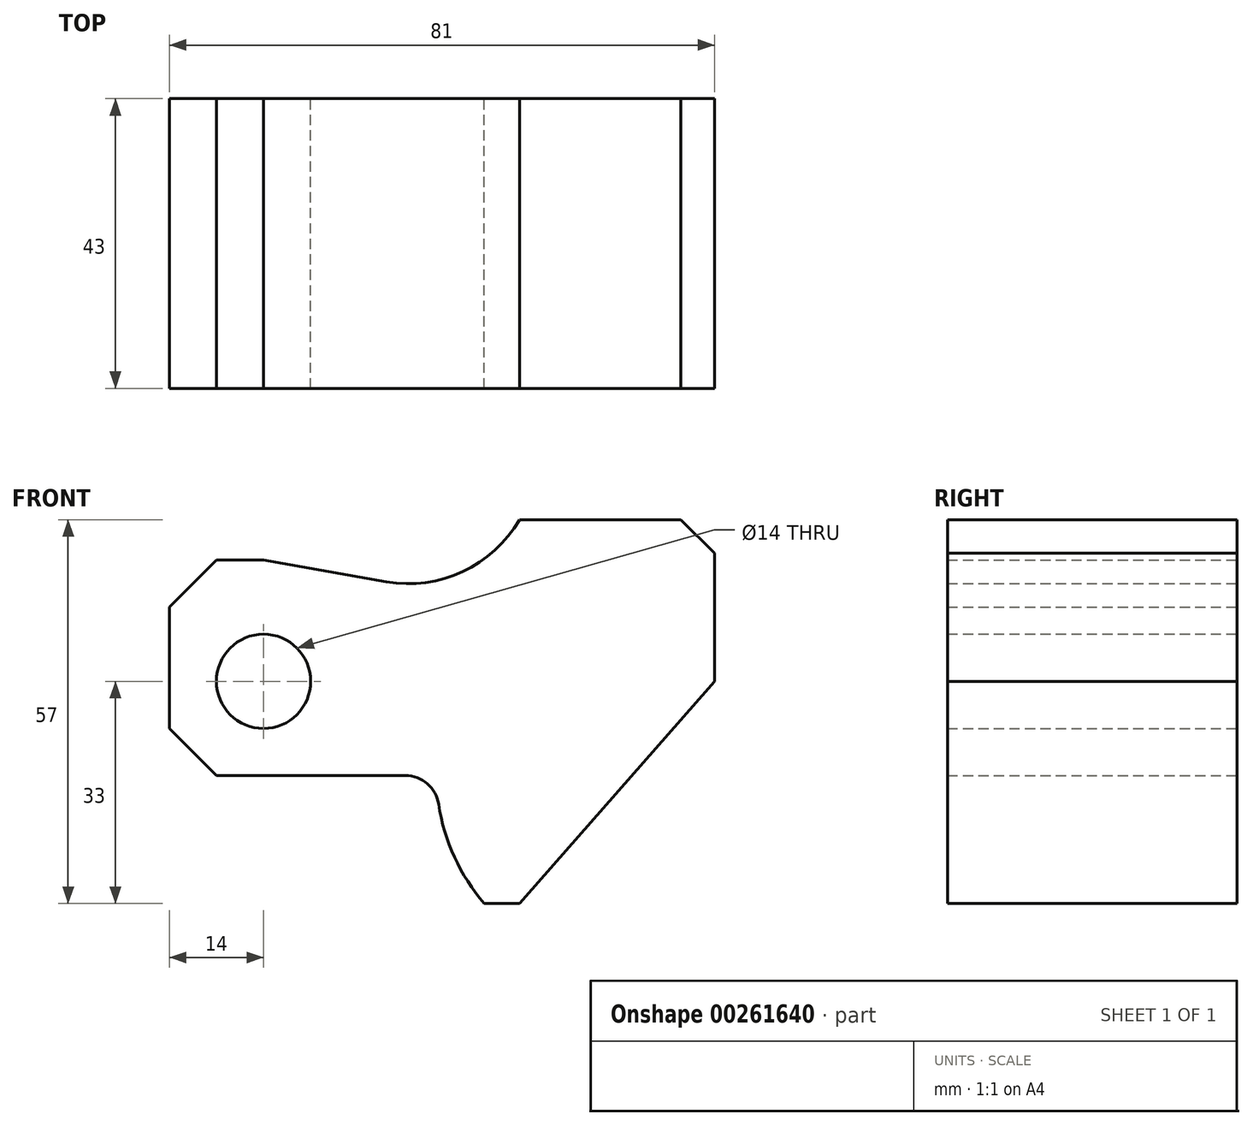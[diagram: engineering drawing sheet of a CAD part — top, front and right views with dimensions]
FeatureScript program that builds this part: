
annotation { "Feature Type Name" : "Feature", "Feature Type Description" : "" }
export const myFeature = defineFeature(function(context is Context, id is Id, definition is map)
    precondition{}
    {
        {
            var Q0;
            Q0=qCreatedBy(makeId("Front.planeOp"),FACE);
            var sketch = newSketch(context, id + "F0", { "sketchPlane" : qUnion([Q0])});
            skLineSegment(sketch, "E0", {"start": v(0, -18.6) * mm, "end": v(0, 28.52) * mm, "construction": true});
            skLineSegment(sketch, "E1", {"start": v(-26.7, 0) * mm, "end": v(26.52, 0) * mm, "construction": true});
            skCircle(sketch, "E2", {"center": v(0, 0) * mm, "radius": 7 * mm});
            skLineSegment(sketch, "E3", {"start": v(-14, 11) * mm, "end": v(-14, -7) * mm});
            skLineSegment(sketch, "E4", {"start": v(-14, -7) * mm, "end": v(-7, -14) * mm});
            skLineSegment(sketch, "E5", {"start": v(-7, -14) * mm, "end": v(21.07, -14) * mm});
            skLineSegment(sketch, "E6", {"start": v(-7, 18) * mm, "end": v(-14, 11) * mm});
            skLineSegment(sketch, "E7", {"start": v(-7, 18) * mm, "end": v(0, 18) * mm});
            skLineSegment(sketch, "E8", {"start": v(0, 18) * mm, "end": v(18.24, 14.78) * mm});
            skLineSegment(sketch, "E9", {"start": v(32.79, -33) * mm, "end": v(38, -33) * mm});
            skLineSegment(sketch, "E10", {"start": v(67, 0) * mm, "end": v(67, 19) * mm});
            skLineSegment(sketch, "E11", {"start": v(62, 24) * mm, "end": v(67, 19) * mm});
            skLineSegment(sketch, "E12", {"start": v(62, 24) * mm, "end": v(38, 24) * mm});
            skLineSegment(sketch, "E13", {"start": v(38, -33) * mm, "end": v(67, 0) * mm});
            skArc(sketch, "E14", {"start": v(18.24, 14.78) * mm, "mid": v(29.57, 16.28) * mm, "end": v(38, 24) * mm});
            skArc(sketch, "E15", {"start": v(26.01, -18.26) * mm, "mid": v(24.33, -15.21) * mm, "end": v(21.07, -14) * mm});
            skArc(sketch, "E16", {"start": v(26.01, -18.26) * mm, "mid": v(28.35, -26.12) * mm, "end": v(32.79, -33) * mm});
            skSolve(sketch);
        }
        {
            var Q0;
            Q0 = qSketchRegion(id + "F0", true);
            extrude(context, id + "F1", {"entities" : qUnion([Q0]), "depth" : 43 * mm});
        }
    });
